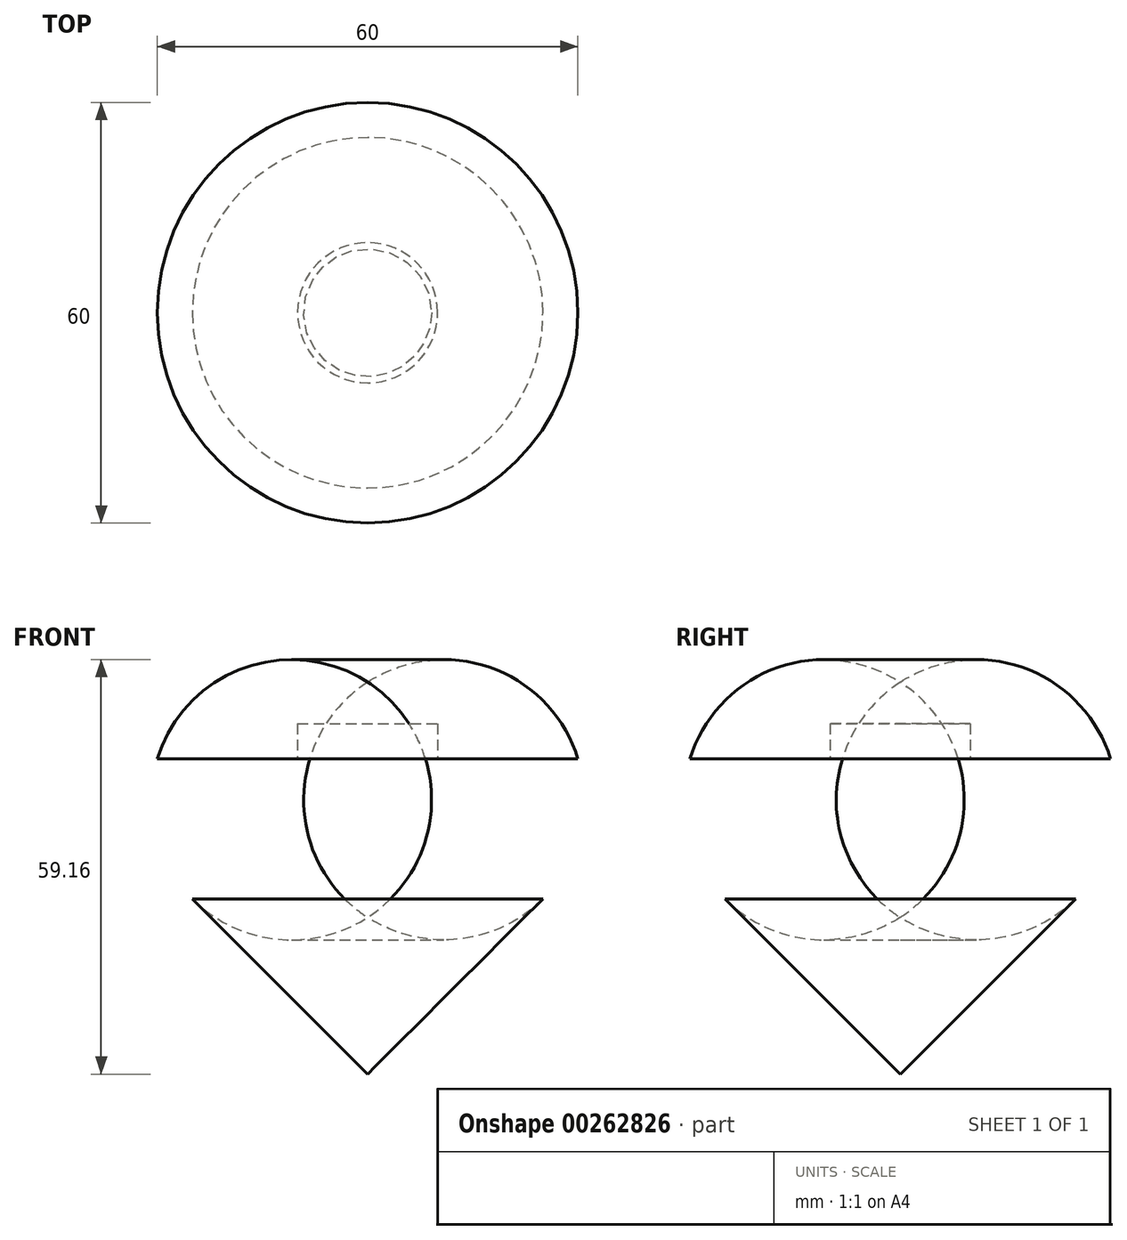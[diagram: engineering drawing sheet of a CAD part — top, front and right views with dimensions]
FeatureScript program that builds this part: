
annotation { "Feature Type Name" : "Feature", "Feature Type Description" : "" }
export const myFeature = defineFeature(function(context is Context, id is Id, definition is map)
    precondition{}
    {
        {
            var Q0;
            Q0=qCreatedBy(makeId("Front.planeOp"),FACE);
            var sketch = newSketch(context, id + "F0", { "sketchPlane" : qUnion([Q0])});
            skLineSegment(sketch, "E0", {"start": v(0, 0) * mm, "end": v(0, 50) * mm});
            skLineSegment(sketch, "E1", {"start": v(0, 50) * mm, "end": v(10, 50) * mm});
            skLineSegment(sketch, "E2", {"start": v(10, 50) * mm, "end": v(10, 45) * mm});
            skLineSegment(sketch, "E3", {"start": v(10, 45) * mm, "end": v(30, 45) * mm});
            skLineSegment(sketch, "E4", {"start": v(0, 0) * mm, "end": v(25.01, 25.01) * mm});
            skArc(sketch, "E5", {"start": v(25.01, 25.01) * mm, "mid": v(30.28, 34.32) * mm, "end": v(30, 45) * mm});
            skSolve(sketch);
        }
        {
            var Q0;
            Q0 = qSketchRegion(id + "F0", true);
            var Q1;
            Q1=sQuery(id+"F0.wireOp",EDGE,"E0");
            revolve(context, id + "F1", {"entities" : qUnion([Q0]), "axis" : qUnion([Q1]), "revolveType" : RevolveType.FULL});
        }
    });
